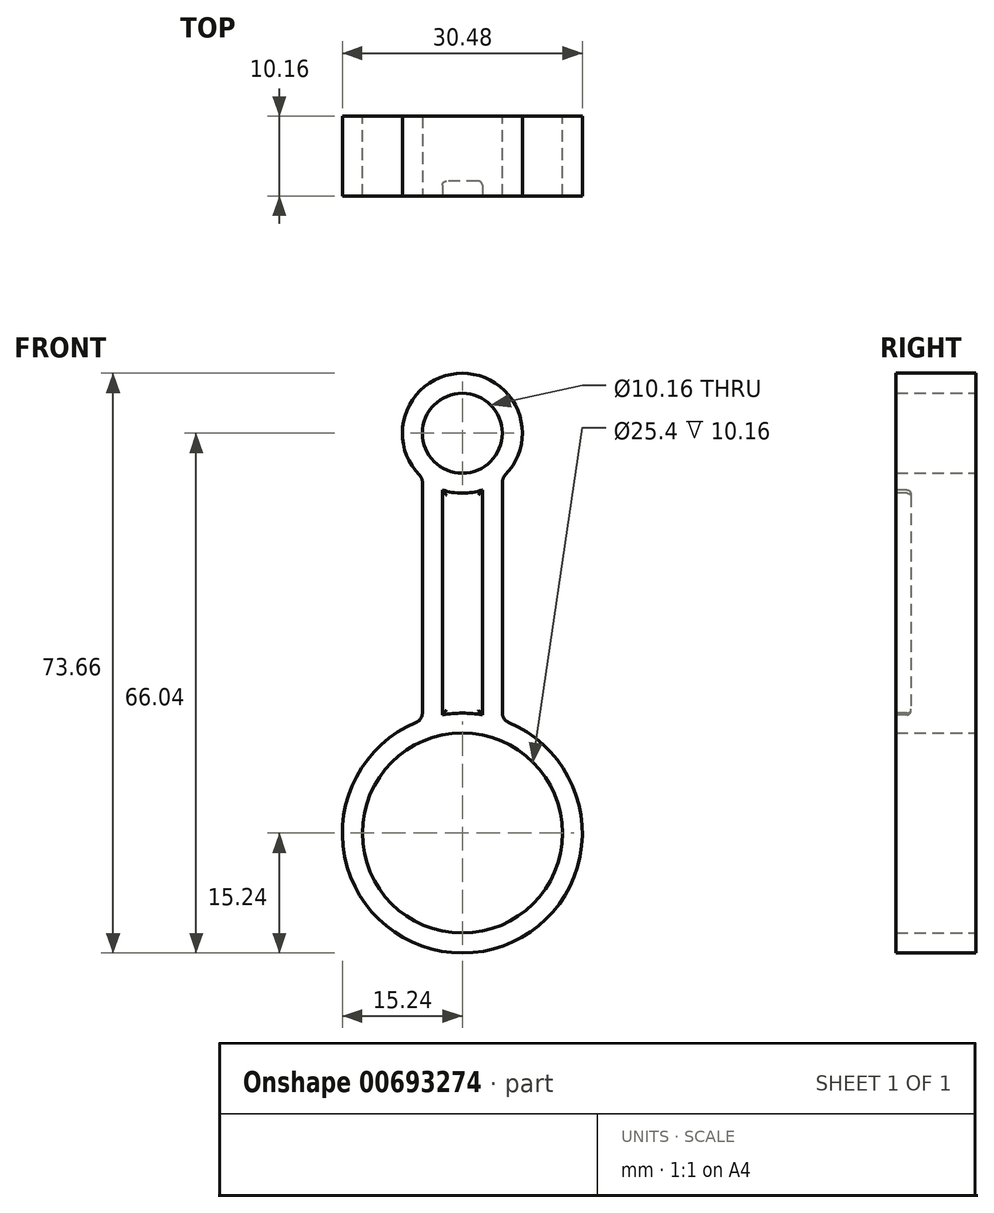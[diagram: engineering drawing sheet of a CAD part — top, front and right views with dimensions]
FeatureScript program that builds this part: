
annotation { "Feature Type Name" : "Feature", "Feature Type Description" : "" }
export const myFeature = defineFeature(function(context is Context, id is Id, definition is map)
    precondition{}
    {
        {
            var Q0;
            Q0=qCreatedBy(makeId("Front.planeOp"),FACE);
            var sketch = newSketch(context, id + "F0", { "sketchPlane" : qUnion([Q0])});
            skCircle(sketch, "E0", {"center": v(0, 25.4) * mm, "radius": 7.62 * mm});
            skCircle(sketch, "E1", {"center": v(0, -25.4) * mm, "radius": 15.24 * mm});
            skLineSegment(sketch, "E2", {"start": v(5.08, 19.72) * mm, "end": v(5.08, -11.03) * mm});
            skCircle(sketch, "E3", {"center": v(0, 25.4) * mm, "radius": 5.08 * mm});
            skCircle(sketch, "E4", {"center": v(0, -25.4) * mm, "radius": 12.7 * mm});
            skLineSegment(sketch, "E5", {"start": v(-5.08, 19.72) * mm, "end": v(-5.08, -11.03) * mm});
            skSolve(sketch);
        }
        {
            var Q0;
            Q0=makeQuery(id+"F0.imprint","IMPRINT",FACE,{"disambiguationData":[TD([[makeQuery(id+"F0.imprint","IMPRINT",EDGE,{"derivedFrom":sQuery(id+"F0.wireOp",EDGE,"E3")}),-1.0]])]});
            var Q1;
            {var subQ0=sQuery(id+"F0.wireOp",EDGE,"E2");Q1=makeQuery(id+"F0.imprint","IMPRINT",FACE,{"disambiguationData":[TD([[makeQuery(id+"F0.imprint","IMPRINT",EDGE,{"derivedFrom":subQ0}),-1.0]])]});}
            var Q2;
            Q2=makeQuery(id+"F0.imprint","IMPRINT",FACE,{"disambiguationData":[TD([[makeQuery(id+"F0.imprint","IMPRINT",EDGE,{"derivedFrom":sQuery(id+"F0.wireOp",EDGE,"E4")}),-1.0]])]});
            extrude(context, id + "F1", {"entities" : qUnion([Q0, Q1, Q2]), "endBound" : BoundingType.SYMMETRIC, "depth" : 10.16 * mm, "offsetDistance" : 25.4 * mm});
        }
        {
            var Q0;
            Q0=makeQuery(id+"F1.opExtrude","SWEPT_EDGE",EDGE,{"disambiguationData":[OSD([sQuery(id+"F0.wireOp",EDGE,"E0"),sQuery(id+"F0.wireOp",EDGE,"E5")])]});
            var Q1;
            Q1=makeQuery(id+"F1.opExtrude","SWEPT_EDGE",EDGE,{"disambiguationData":[OSD([sQuery(id+"F0.wireOp",EDGE,"E1"),sQuery(id+"F0.wireOp",EDGE,"E5")])]});
            var Q2;
            Q2=makeQuery(id+"F1.opExtrude","SWEPT_EDGE",EDGE,{"disambiguationData":[OSD([sQuery(id+"F0.wireOp",EDGE,"E0"),sQuery(id+"F0.wireOp",EDGE,"E2")])]});
            var Q3;
            Q3=makeQuery(id+"F1.opExtrude","SWEPT_EDGE",EDGE,{"disambiguationData":[OSD([sQuery(id+"F0.wireOp",EDGE,"E1"),sQuery(id+"F0.wireOp",EDGE,"E2")])]});
            fillet(context, id + "F2", {"entities" : qUnion([Q0, Q1, Q2, Q3]), "radius" : 1.27 * mm, "tangentPropagation" : true, "allowEdgeOverflow" : false});
        }
        {
            var Q0;
            Q0=makeQuery(id+"F1.opExtrude","CAP_FACE",FACE,{"disambiguationData":[OSD([sQuery(id+"F0.wireOp",EDGE,"E0"),sQuery(id+"F0.wireOp",EDGE,"E1"),sQuery(id+"F0.wireOp",EDGE,"E2"),sQuery(id+"F0.wireOp",EDGE,"E3"),sQuery(id+"F0.wireOp",EDGE,"E4"),sQuery(id+"F0.wireOp",EDGE,"E5")])],"isStart":false});
            var sketch = newSketch(context, id + "F3", { "sketchPlane" : qUnion([Q0])});
            skLineSegment(sketch, "E6", {"start": v(-2.54, 18.22) * mm, "end": v(-2.54, -10.37) * mm});
            skLineSegment(sketch, "E7", {"start": v(2.54, 18.22) * mm, "end": v(2.54, -10.37) * mm});
            skArc(sketch, "E8", {"start": v(-2.54, -10.37) * mm, "mid": v(0, -10.16) * mm, "end": v(2.54, -10.37) * mm});
            skArc(sketch, "E9", {"start": v(-2.54, 18.22) * mm, "mid": v(0, 17.78) * mm, "end": v(2.54, 18.22) * mm});
            skSolve(sketch);
        }
        {
            var Q0;
            Q0=makeQuery(id+"F3.imprint","IMPRINT",FACE,{"disambiguationData":[TD([[makeQuery(id+"F3.imprint","IMPRINT",EDGE,{"derivedFrom":sQuery(id+"F3.wireOp",EDGE,"E6")}),1.0]])]});
            extrude(context, id + "F4", {"entities" : qUnion([Q0]), "operationType" : NewBodyOperationType.REMOVE, "oppositeDirection" : true, "depth" : 1.9 * mm, "offsetDistance" : 25.4 * mm});
        }
        {
            var Q0;
            Q0=makeQuery(id+"F4.boolean.opBoolean","COPY",EDGE,{"derivedFrom":makeQuery(id+"F4.opExtrude","CAP_EDGE",EDGE,{"disambiguationData":[OSD([sQuery(id+"F3.wireOp",EDGE,"E6")])],"isStart":false})});
            var Q1;
            Q1=makeQuery(id+"F4.boolean.opBoolean","COPY",EDGE,{"derivedFrom":makeQuery(id+"F4.opExtrude","CAP_EDGE",EDGE,{"disambiguationData":[OSD([sQuery(id+"F3.wireOp",EDGE,"E9")])],"isStart":false})});
            var Q2;
            Q2=makeQuery(id+"F4.boolean.opBoolean","COPY",EDGE,{"derivedFrom":makeQuery(id+"F4.opExtrude","CAP_EDGE",EDGE,{"disambiguationData":[OSD([sQuery(id+"F3.wireOp",EDGE,"E7")])],"isStart":false})});
            var Q3;
            Q3=makeQuery(id+"F4.boolean.opBoolean","COPY",EDGE,{"derivedFrom":makeQuery(id+"F4.opExtrude","CAP_EDGE",EDGE,{"disambiguationData":[OSD([sQuery(id+"F3.wireOp",EDGE,"E8")])],"isStart":false})});
            var Q4;
            Q4=makeQuery(id+"Fqrs4vDNRQKkKW1_1.1.F4.boolean.opBoolean","COPY",EDGE,{"derivedFrom":makeQuery(id+"Fqrs4vDNRQKkKW1_1.1.F4.opExtrude","CAP_EDGE",EDGE,{"disambiguationData":[OSD([sQuery(id+"F3.wireOp",EDGE,"E8")])],"isStart":false})});
            var Q5;
            Q5=makeQuery(id+"Fqrs4vDNRQKkKW1_1.1.F4.boolean.opBoolean","COPY",EDGE,{"derivedFrom":makeQuery(id+"Fqrs4vDNRQKkKW1_1.1.F4.opExtrude","SWEPT_EDGE",EDGE,{"disambiguationData":[OSD([sQuery(id+"F3.wireOp",EDGE,"E7"),sQuery(id+"F3.wireOp",EDGE,"E8")])]})});
            var Q6;
            Q6=makeQuery(id+"Fqrs4vDNRQKkKW1_1.1.F4.boolean.opBoolean","COPY",EDGE,{"derivedFrom":makeQuery(id+"Fqrs4vDNRQKkKW1_1.1.F4.opExtrude","CAP_EDGE",EDGE,{"disambiguationData":[OSD([sQuery(id+"F3.wireOp",EDGE,"E7")])],"isStart":false})});
            var Q7;
            Q7=makeQuery(id+"Fqrs4vDNRQKkKW1_1.1.F4.boolean.opBoolean","COPY",EDGE,{"derivedFrom":makeQuery(id+"Fqrs4vDNRQKkKW1_1.1.F4.opExtrude","CAP_EDGE",EDGE,{"disambiguationData":[OSD([sQuery(id+"F3.wireOp",EDGE,"E6")])],"isStart":false})});
            var Q8;
            Q8=makeQuery(id+"Fqrs4vDNRQKkKW1_1.1.F4.boolean.opBoolean","COPY",EDGE,{"derivedFrom":makeQuery(id+"Fqrs4vDNRQKkKW1_1.1.F4.opExtrude","SWEPT_EDGE",EDGE,{"disambiguationData":[OSD([sQuery(id+"F3.wireOp",EDGE,"E6"),sQuery(id+"F3.wireOp",EDGE,"E8")])]})});
            var Q9;
            Q9=makeQuery(id+"Fqrs4vDNRQKkKW1_1.1.F4.boolean.opBoolean","COPY",EDGE,{"derivedFrom":makeQuery(id+"Fqrs4vDNRQKkKW1_1.1.F4.opExtrude","SWEPT_EDGE",EDGE,{"disambiguationData":[OSD([sQuery(id+"F3.wireOp",EDGE,"E7"),sQuery(id+"F3.wireOp",EDGE,"E9")])]})});
            var Q10;
            Q10=makeQuery(id+"Fqrs4vDNRQKkKW1_1.1.F4.boolean.opBoolean","COPY",EDGE,{"derivedFrom":makeQuery(id+"Fqrs4vDNRQKkKW1_1.1.F4.opExtrude","CAP_EDGE",EDGE,{"disambiguationData":[OSD([sQuery(id+"F3.wireOp",EDGE,"E9")])],"isStart":false})});
            var Q11;
            Q11=makeQuery(id+"Fqrs4vDNRQKkKW1_1.1.F4.boolean.opBoolean","COPY",EDGE,{"derivedFrom":makeQuery(id+"Fqrs4vDNRQKkKW1_1.1.F4.opExtrude","SWEPT_EDGE",EDGE,{"disambiguationData":[OSD([sQuery(id+"F3.wireOp",EDGE,"E6"),sQuery(id+"F3.wireOp",EDGE,"E9")])]})});
            fillet(context, id + "F5", {"entities" : qUnion([Q0, Q1, Q2, Q3, Q4, Q5, Q6, Q7, Q8, Q9, Q10, Q11]), "radius" : 0.5 * mm, "tangentPropagation" : true, "allowEdgeOverflow" : false});
        }
    });
